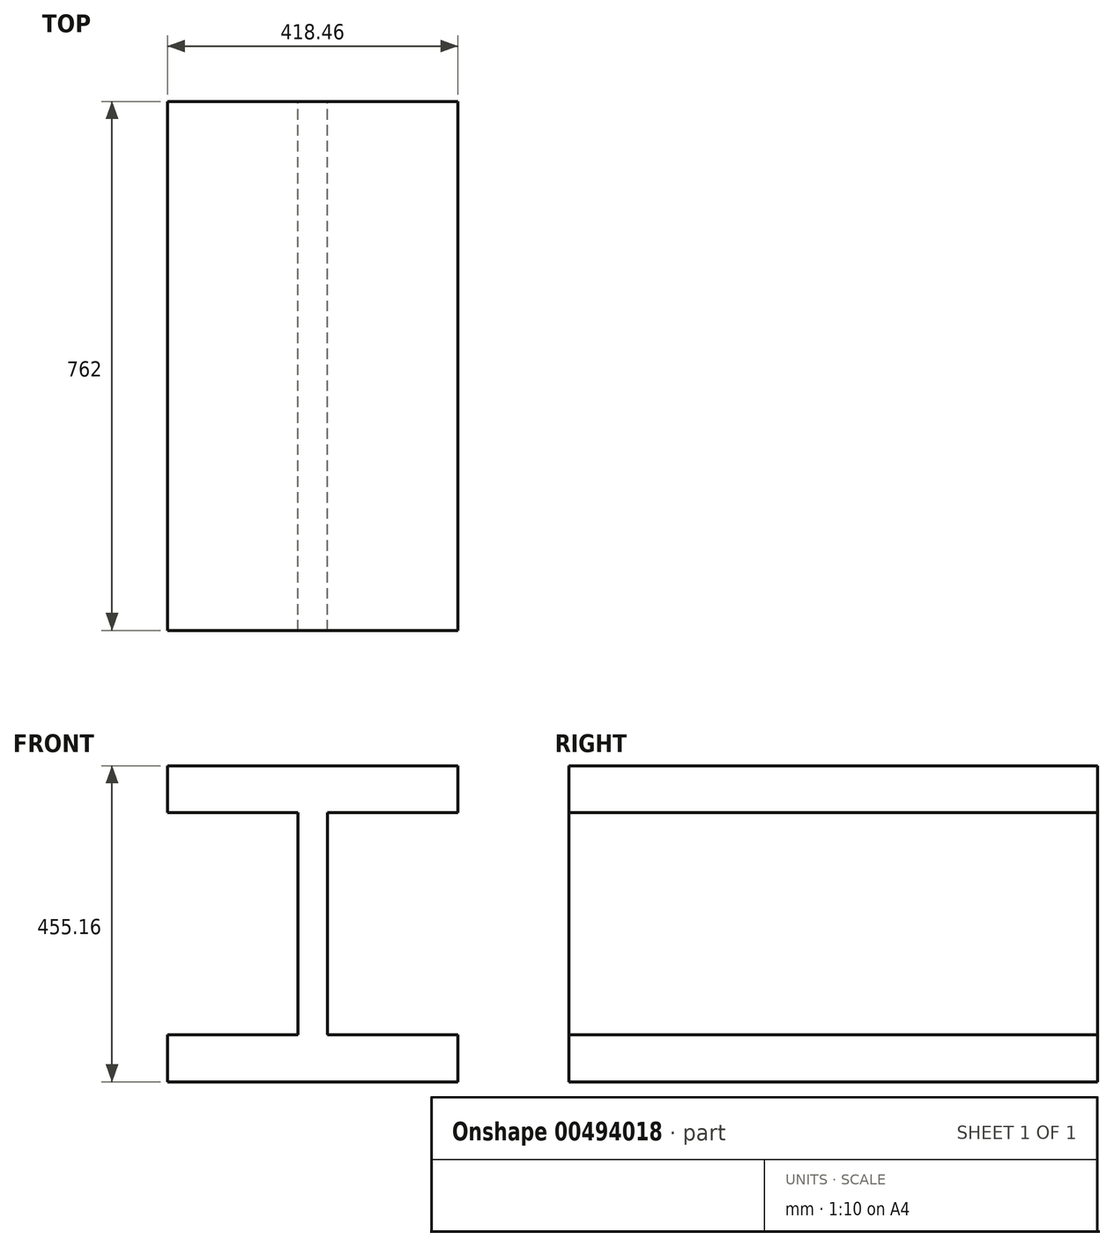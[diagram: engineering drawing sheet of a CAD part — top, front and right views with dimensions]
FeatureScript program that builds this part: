
annotation { "Feature Type Name" : "Feature", "Feature Type Description" : "" }
export const myFeature = defineFeature(function(context is Context, id is Id, definition is map)
    precondition{}
    {
        {
            var Q0;
            Q0=qCreatedBy(makeId("Front.planeOp"),FACE);
            var sketch = newSketch(context, id + "F0", { "sketchPlane" : qUnion([Q0])});
            skLineSegment(sketch, "E0", {"start": v(0, -428.52) * mm, "end": v(0, 307.08) * mm, "construction": true});
            skLineSegment(sketch, "E1", {"start": v(432.9, 0) * mm, "end": v(-493.72, 0) * mm, "construction": true});
            skLineSegment(sketch, "E2.bottom", {"start": v(-21.02, 160.02) * mm, "end": v(21.02, 160.02) * mm});
            skLineSegment(sketch, "E2.top", {"start": v(-21.02, -160.02) * mm, "end": v(21.02, -160.02) * mm});
            skLineSegment(sketch, "E2.left", {"start": v(-21.02, 160.02) * mm, "end": v(-21.02, -160.02) * mm});
            skLineSegment(sketch, "E2.right", {"start": v(21.02, 160.02) * mm, "end": v(21.02, -160.02) * mm});
            skPoint(sketch, "E2.middle", {"position": v(0, 0) * mm});
            skLineSegment(sketch, "E3.bottom", {"start": v(-209.23, 160.02) * mm, "end": v(209.23, 160.02) * mm});
            skLineSegment(sketch, "E3.top", {"start": v(-209.23, 227.58) * mm, "end": v(209.23, 227.58) * mm});
            skLineSegment(sketch, "E3.left", {"start": v(-209.23, 160.02) * mm, "end": v(-209.23, 227.58) * mm});
            skLineSegment(sketch, "E3.right", {"start": v(209.23, 160.02) * mm, "end": v(209.23, 227.58) * mm});
            skPoint(sketch, "E3.middle", {"position": v(0, 193.8) * mm});
            skLineSegment(sketch, "E4.bottom", {"start": v(-209.23, -160.02) * mm, "end": v(209.23, -160.02) * mm});
            skLineSegment(sketch, "E4.top", {"start": v(-209.23, -227.58) * mm, "end": v(209.23, -227.58) * mm});
            skLineSegment(sketch, "E4.left", {"start": v(-209.23, -160.02) * mm, "end": v(-209.23, -227.58) * mm});
            skLineSegment(sketch, "E4.right", {"start": v(209.23, -160.02) * mm, "end": v(209.23, -227.58) * mm});
            skPoint(sketch, "E4.middle", {"position": v(0, -193.8) * mm});
            skPoint(sketch, "E4.cornerSnap0", {"position": v(0, -160.02) * mm});
            skSolve(sketch);
        }
        {
            var Q0;
            Q0=qSketchRegion(id+"F0",true);
            extrude(context, id + "F1", {"entities" : qUnion([Q0]), "depth" : 762 * mm});
        }
    });
